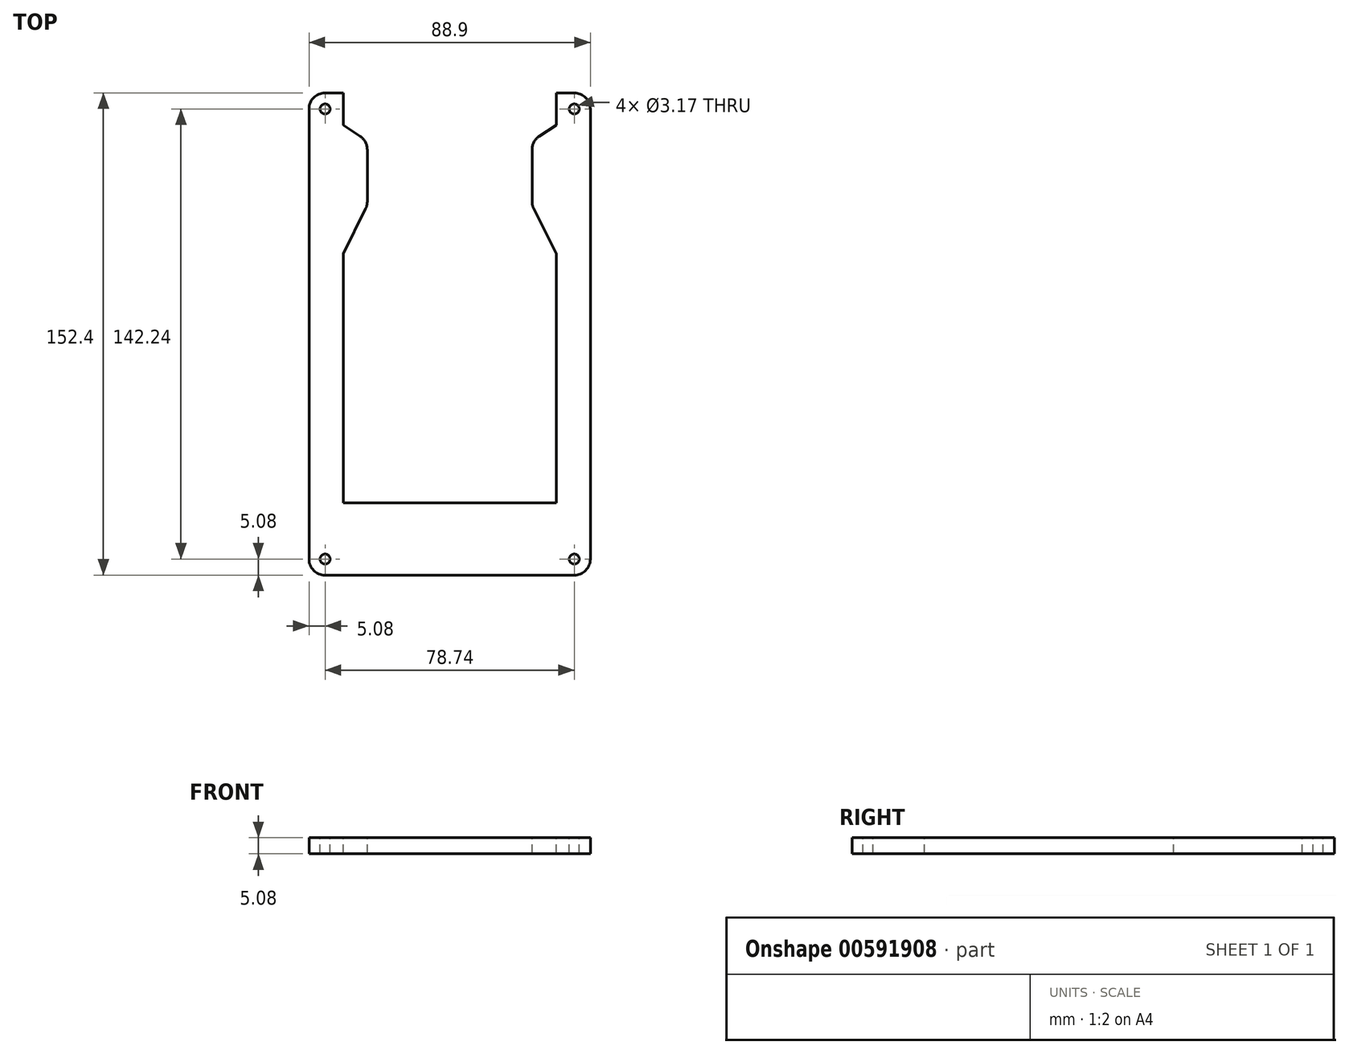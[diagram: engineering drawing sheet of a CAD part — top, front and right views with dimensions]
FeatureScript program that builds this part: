
annotation { "Feature Type Name" : "Feature", "Feature Type Description" : "" }
export const myFeature = defineFeature(function(context is Context, id is Id, definition is map)
    precondition{}
    {
        {
            var Q0;
            Q0=qCreatedBy(makeId("Top.planeOp"),FACE);
            var sketch = newSketch(context, id + "F0", { "sketchPlane" : qUnion([Q0])});
            skLineSegment(sketch, "E0.bottom", {"start": v(0, 0) * mm, "end": v(88.9, 0) * mm});
            skLineSegment(sketch, "E0.top", {"start": v(0, -152.4) * mm, "end": v(88.9, -152.4) * mm});
            skLineSegment(sketch, "E0.left", {"start": v(0, 0) * mm, "end": v(0, -152.4) * mm});
            skLineSegment(sketch, "E0.right", {"start": v(88.9, 0) * mm, "end": v(88.9, -152.4) * mm});
            skSolve(sketch);
        }
        {
            var Q0;
            Q0=makeQuery(id+"F0.imprint","IMPRINT",FACE,{"disambiguationData":[TD([[makeQuery(id+"F0.imprint","IMPRINT",EDGE,{"derivedFrom":sQuery(id+"F0.wireOp",EDGE,"E0.bottom")}),-1.0]])]});
            extrude(context, id + "F1", {"entities" : qUnion([Q0]), "depth" : 5.08 * mm, "offsetDistance" : 25.4 * mm});
        }
        {
            var Q0;
            Q0=makeQuery(id+"F1.opExtrude","CAP_FACE",FACE,{"disambiguationData":[OSD([sQuery(id+"F0.wireOp",EDGE,"E0.bottom"),sQuery(id+"F0.wireOp",EDGE,"E0.top"),sQuery(id+"F0.wireOp",EDGE,"E0.left"),sQuery(id+"F0.wireOp",EDGE,"E0.right")])],"isStart":false});
            var sketch = newSketch(context, id + "F2", { "sketchPlane" : qUnion([Q0])});
            skLineSegment(sketch, "E1.bottom", {"start": v(10.8, 0) * mm, "end": v(78.1, 0) * mm});
            skLineSegment(sketch, "E1.top", {"start": v(10.8, -129.54) * mm, "end": v(78.1, -129.54) * mm});
            skLineSegment(sketch, "E1.left", {"start": v(10.8, 0) * mm, "end": v(10.8, -10.16) * mm});
            skLineSegment(sketch, "E1.right", {"start": v(78.1, 0) * mm, "end": v(78.1, -10.16) * mm});
            skLineSegment(sketch, "E2", {"start": v(10.8, -10.16) * mm, "end": v(18.41, -15.24) * mm});
            skLineSegment(sketch, "E3", {"start": v(18.41, -15.24) * mm, "end": v(18.41, -35.56) * mm});
            skLineSegment(sketch, "E4", {"start": v(18.41, -35.56) * mm, "end": v(10.8, -50.8) * mm});
            skLineSegment(sketch, "E5", {"start": v(78.1, -10.16) * mm, "end": v(70.48, -15.24) * mm});
            skLineSegment(sketch, "E6", {"start": v(70.48, -15.24) * mm, "end": v(70.48, -35.56) * mm});
            skLineSegment(sketch, "E7", {"start": v(70.48, -35.56) * mm, "end": v(78.1, -50.8) * mm});
            skLineSegment(sketch, "E8.trimOffspring", {"start": v(10.8, -50.8) * mm, "end": v(10.8, -129.54) * mm});
            skLineSegment(sketch, "E9.trimOffspring", {"start": v(78.1, -50.8) * mm, "end": v(78.1, -129.54) * mm});
            skSolve(sketch);
        }
        {
            var Q0;
            Q0=makeQuery(id+"F2.imprint","IMPRINT",FACE,{"disambiguationData":[TD([[makeQuery(id+"F2.imprint","IMPRINT",EDGE,{"derivedFrom":sQuery(id+"F2.wireOp",EDGE,"E1.bottom")}),-1.0]])]});
            extrude(context, id + "F3", {"entities" : qUnion([Q0]), "operationType" : NewBodyOperationType.REMOVE, "oppositeDirection" : true, "depth" : 25.4 * mm, "offsetDistance" : 25.4 * mm});
        }
        {
            var Q0;
            Q0=makeQuery(id+"F1.opExtrude","CAP_FACE",FACE,{"disambiguationData":[OSD([sQuery(id+"F0.wireOp",EDGE,"E0.bottom"),sQuery(id+"F0.wireOp",EDGE,"E0.top"),sQuery(id+"F0.wireOp",EDGE,"E0.left"),sQuery(id+"F0.wireOp",EDGE,"E0.right")])],"isStart":false});
            var sketch = newSketch(context, id + "F4", { "sketchPlane" : qUnion([Q0])});
            skCircle(sketch, "E10", {"center": v(5.08, -5.08) * mm, "radius": 1.59 * mm});
            skCircle(sketch, "E11", {"center": v(5.08, -147.32) * mm, "radius": 1.59 * mm});
            skCircle(sketch, "E12", {"center": v(83.82, -147.32) * mm, "radius": 1.59 * mm});
            skCircle(sketch, "E13", {"center": v(83.82, -5.08) * mm, "radius": 1.59 * mm});
            skSolve(sketch);
        }
        {
            var Q0;
            Q0=makeQuery(id+"F4.imprint","IMPRINT",FACE,{"disambiguationData":[TD([[makeQuery(id+"F4.imprint","IMPRINT",EDGE,{"derivedFrom":sQuery(id+"F4.wireOp",EDGE,"E10")}),1.0]])]});
            var Q1;
            Q1=makeQuery(id+"F4.imprint","IMPRINT",FACE,{"disambiguationData":[TD([[makeQuery(id+"F4.imprint","IMPRINT",EDGE,{"derivedFrom":sQuery(id+"F4.wireOp",EDGE,"E13")}),1.0]])]});
            var Q2;
            Q2=makeQuery(id+"F4.imprint","IMPRINT",FACE,{"disambiguationData":[TD([[makeQuery(id+"F4.imprint","IMPRINT",EDGE,{"derivedFrom":sQuery(id+"F4.wireOp",EDGE,"E12")}),1.0]])]});
            var Q3;
            Q3=makeQuery(id+"F4.imprint","IMPRINT",FACE,{"disambiguationData":[TD([[makeQuery(id+"F4.imprint","IMPRINT",EDGE,{"derivedFrom":sQuery(id+"F4.wireOp",EDGE,"E11")}),1.0]])]});
            extrude(context, id + "F5", {"entities" : qUnion([Q0, Q1, Q2, Q3]), "operationType" : NewBodyOperationType.REMOVE, "oppositeDirection" : true, "depth" : 25.4 * mm, "offsetDistance" : 25.4 * mm});
        }
        {
            var Q0;
            Q0=makeQuery(id+"F1.opExtrude","SWEPT_EDGE",EDGE,{"disambiguationData":[OSD([sQuery(id+"F0.wireOp",EDGE,"E0.top"),sQuery(id+"F0.wireOp",EDGE,"E0.right")])]});
            var Q1;
            Q1=makeQuery(id+"F1.opExtrude","SWEPT_EDGE",EDGE,{"disambiguationData":[OSD([sQuery(id+"F0.wireOp",EDGE,"E0.top"),sQuery(id+"F0.wireOp",EDGE,"E0.left")])]});
            var Q2;
            Q2=makeQuery(id+"F1.opExtrude","SWEPT_EDGE",EDGE,{"disambiguationData":[OSD([sQuery(id+"F0.wireOp",EDGE,"E0.bottom"),sQuery(id+"F0.wireOp",EDGE,"E0.right")])]});
            var Q3;
            Q3=makeQuery(id+"F1.opExtrude","SWEPT_EDGE",EDGE,{"disambiguationData":[OSD([sQuery(id+"F0.wireOp",EDGE,"E0.bottom"),sQuery(id+"F0.wireOp",EDGE,"E0.left")])]});
            var Q4;
            Q4=makeQuery(id+"F3.boolean.opBoolean","COPY",EDGE,{"derivedFrom":makeQuery(id+"F3.opExtrude","SWEPT_EDGE",EDGE,{"disambiguationData":[OSD([sQuery(id+"F2.wireOp",EDGE,"E2"),sQuery(id+"F2.wireOp",EDGE,"E3")])]})});
            var Q5;
            Q5=makeQuery(id+"F3.boolean.opBoolean","COPY",EDGE,{"derivedFrom":makeQuery(id+"F3.opExtrude","SWEPT_EDGE",EDGE,{"disambiguationData":[OSD([sQuery(id+"F2.wireOp",EDGE,"E3"),sQuery(id+"F2.wireOp",EDGE,"E4")])]})});
            var Q6;
            Q6=makeQuery(id+"F3.boolean.opBoolean","COPY",EDGE,{"derivedFrom":makeQuery(id+"F3.opExtrude","SWEPT_EDGE",EDGE,{"disambiguationData":[OSD([sQuery(id+"F2.wireOp",EDGE,"E6"),sQuery(id+"F2.wireOp",EDGE,"E7")])]})});
            var Q7;
            Q7=makeQuery(id+"F3.boolean.opBoolean","COPY",EDGE,{"derivedFrom":makeQuery(id+"F3.opExtrude","SWEPT_EDGE",EDGE,{"disambiguationData":[OSD([sQuery(id+"F2.wireOp",EDGE,"E5"),sQuery(id+"F2.wireOp",EDGE,"E6")])]})});
            fillet(context, id + "F6", {"entities" : qUnion([Q0, Q1, Q2, Q3, Q4, Q5, Q6, Q7]), "tangentPropagation" : true, "radius" : 5.08 * mm, "defaultsChanged" : false, "vertexSettings" : [], "allowEdgeOverflow" : false});
        }
    });
